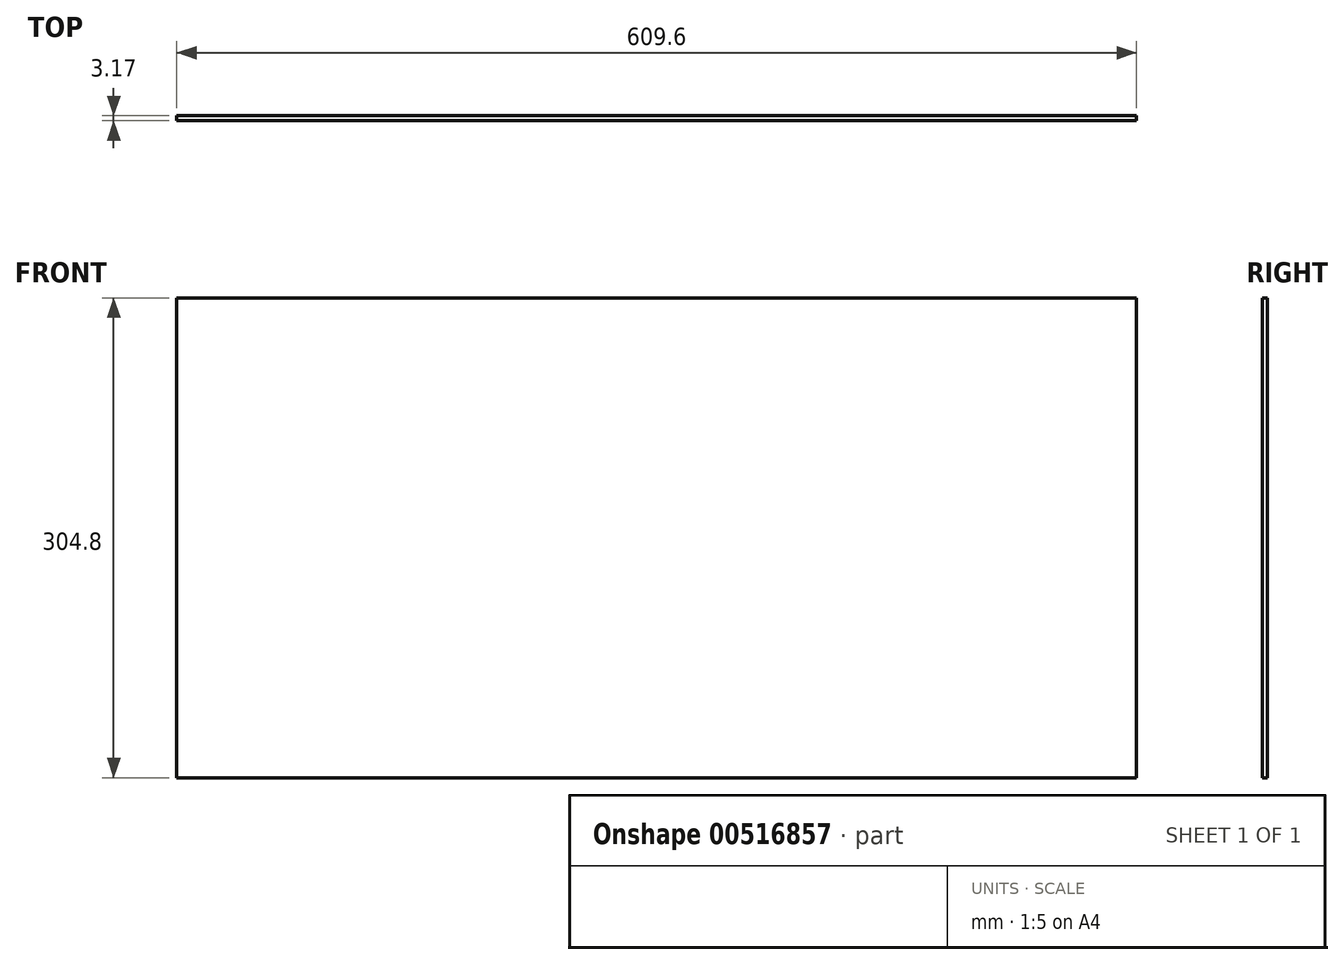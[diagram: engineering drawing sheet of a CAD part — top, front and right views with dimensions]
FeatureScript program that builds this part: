
annotation { "Feature Type Name" : "Feature", "Feature Type Description" : "" }
export const myFeature = defineFeature(function(context is Context, id is Id, definition is map)
    precondition{}
    {
        {
            var Q0;
            Q0=qCreatedBy(makeId("Front.planeOp"),FACE);
            var sketch = newSketch(context, id + "F0", { "sketchPlane" : qUnion([Q0])});
            skLineSegment(sketch, "E0.bottom", {"start": v(-105.81, 43.62) * mm, "end": v(503.79, 43.62) * mm});
            skLineSegment(sketch, "E0.top", {"start": v(-105.81, -261.18) * mm, "end": v(503.79, -261.18) * mm});
            skLineSegment(sketch, "E0.left", {"start": v(-105.81, 43.62) * mm, "end": v(-105.81, -261.18) * mm});
            skLineSegment(sketch, "E0.right", {"start": v(503.79, 43.62) * mm, "end": v(503.79, -261.18) * mm});
            skSolve(sketch);
        }
        {
            var Q0;
            Q0 = qSketchRegion(id + "F0", true);
            extrude(context, id + "F1", {"entities" : qUnion([Q0]), "depth" : 3.17 * mm, "offsetDistance" : 25.4 * mm});
        }
    });
